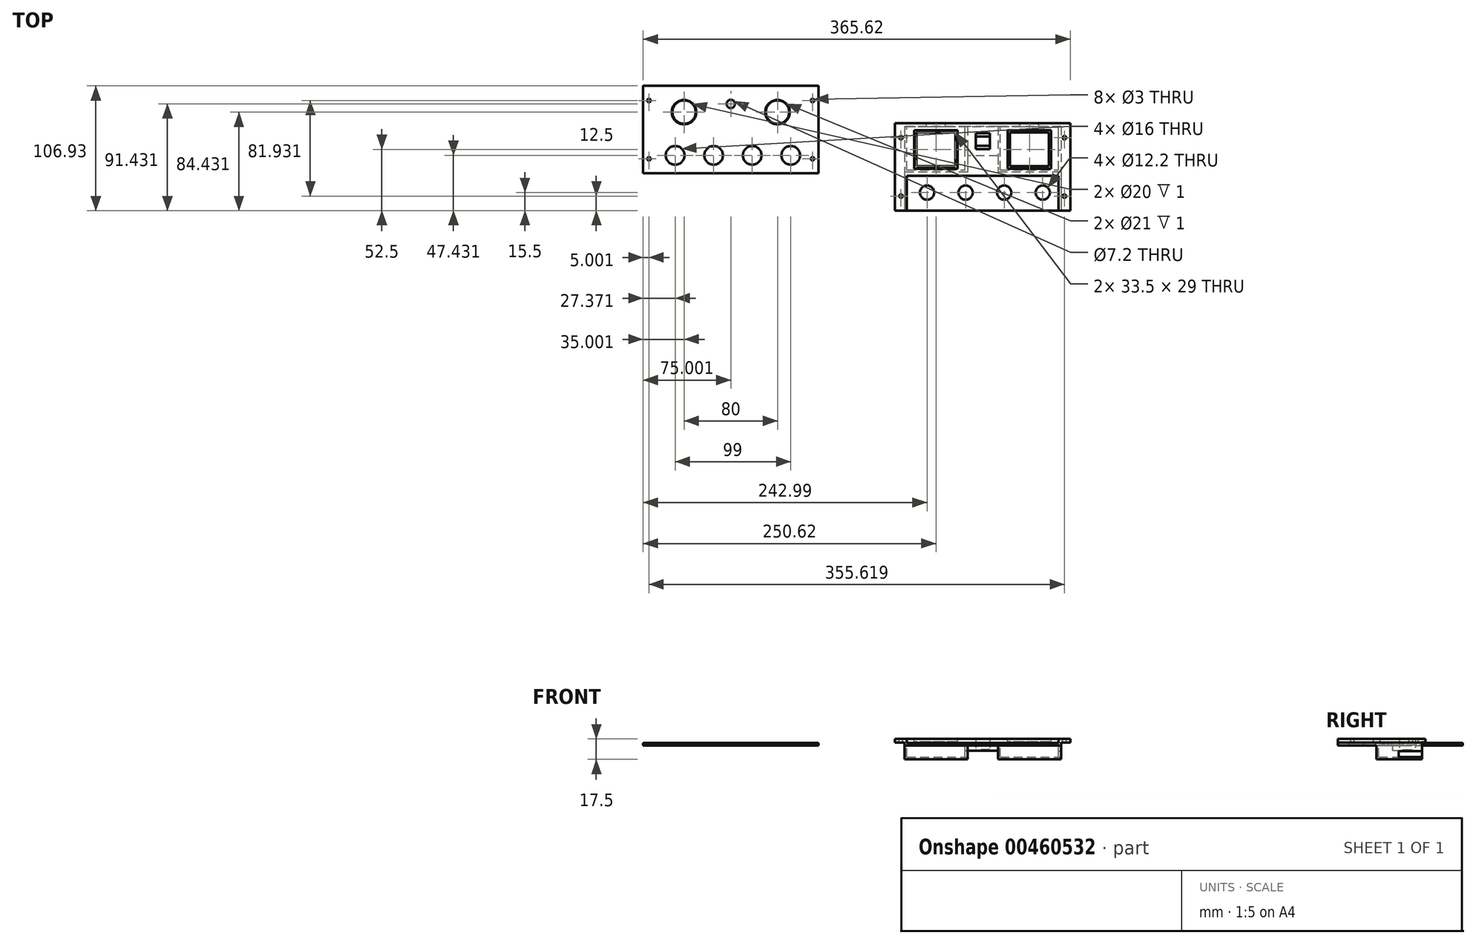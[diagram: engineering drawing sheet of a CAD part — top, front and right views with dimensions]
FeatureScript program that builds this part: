
annotation { "Feature Type Name" : "Feature", "Feature Type Description" : "" }
export const myFeature = defineFeature(function(context is Context, id is Id, definition is map)
    precondition{}
    {
        {
            var Q0;
            Q0=qCreatedBy(makeId("Top.planeOp"),FACE);
            var sketch = newSketch(context, id + "F0", { "sketchPlane" : qUnion([Q0])});
            skLineSegment(sketch, "E0.bottom", {"start": v(75, -37.5) * mm, "end": v(-75, -37.5) * mm});
            skLineSegment(sketch, "E0.top", {"start": v(75, 37.5) * mm, "end": v(-75, 37.5) * mm});
            skLineSegment(sketch, "E0.left", {"start": v(75, -37.5) * mm, "end": v(75, 37.5) * mm});
            skLineSegment(sketch, "E0.right", {"start": v(-75, -37.5) * mm, "end": v(-75, 37.5) * mm});
            skPoint(sketch, "E0.middle", {"position": v(0, 0) * mm});
            skCircle(sketch, "E1", {"center": v(0, 22) * mm, "radius": 5 * mm, "construction": true});
            skCircle(sketch, "E2", {"center": v(-47.63, -22) * mm, "radius": 6.1 * mm});
            skCircle(sketch, "E3.1.0.0", {"center": v(-14.63, -22) * mm, "radius": 6.1 * mm});
            skCircle(sketch, "E3.2.0.0", {"center": v(18.37, -22) * mm, "radius": 6.1 * mm});
            skCircle(sketch, "E3.3.0.0", {"center": v(51.37, -22) * mm, "radius": 6.1 * mm});
            skLineSegment(sketch, "E3.direction1", {"start": v(-47.63, -22) * mm, "end": v(-14.63, -22) * mm, "construction": true});
            skLineSegment(sketch, "E4.bottom", {"start": v(-75, 37.5) * mm, "end": v(-65, 37.5) * mm, "construction": true});
            skLineSegment(sketch, "E4.top", {"start": v(-75, -37.5) * mm, "end": v(-65, -37.5) * mm, "construction": true});
            skLineSegment(sketch, "E4.left", {"start": v(-75, 37.5) * mm, "end": v(-75, -37.5) * mm, "construction": true});
            skLineSegment(sketch, "E4.right", {"start": v(-65, 37.5) * mm, "end": v(-65, -37.5) * mm, "construction": true});
            skLineSegment(sketch, "E5.bottom", {"start": v(75, 37.5) * mm, "end": v(65, 37.5) * mm, "construction": true});
            skLineSegment(sketch, "E5.top", {"start": v(75, -37.5) * mm, "end": v(65, -37.5) * mm, "construction": true});
            skLineSegment(sketch, "E5.left", {"start": v(75, 37.5) * mm, "end": v(75, -37.5) * mm, "construction": true});
            skLineSegment(sketch, "E5.right", {"start": v(65, 37.5) * mm, "end": v(65, -37.5) * mm, "construction": true});
            skPoint(sketch, "E6.middle", {"position": v(-40, 15) * mm});
            skLineSegment(sketch, "E7.bottom", {"start": v(-23.25, 0.5) * mm, "end": v(-56.75, 0.5) * mm});
            skLineSegment(sketch, "E7.top", {"start": v(-23.25, 29.5) * mm, "end": v(-56.75, 29.5) * mm});
            skLineSegment(sketch, "E7.left", {"start": v(-23.25, 0.5) * mm, "end": v(-23.25, 29.5) * mm});
            skLineSegment(sketch, "E7.right", {"start": v(-56.75, 0.5) * mm, "end": v(-56.75, 29.5) * mm});
            skLineSegment(sketch, "E8.bottom", {"start": v(56.75, 0.5) * mm, "end": v(23.25, 0.5) * mm});
            skLineSegment(sketch, "E8.top", {"start": v(56.75, 29.5) * mm, "end": v(23.25, 29.5) * mm});
            skLineSegment(sketch, "E8.left", {"start": v(56.75, 0.5) * mm, "end": v(56.75, 29.5) * mm});
            skLineSegment(sketch, "E8.right", {"start": v(23.25, 0.5) * mm, "end": v(23.25, 29.5) * mm});
            skPoint(sketch, "E8.middle", {"position": v(40, 15) * mm});
            skPoint(sketch, "E9.centerSnap0", {"position": v(-70, 37.5) * mm});
            skCircle(sketch, "E10", {"center": v(-70, 25) * mm, "radius": 1.5 * mm});
            skCircle(sketch, "E11", {"center": v(-70, -25) * mm, "radius": 1.5 * mm});
            skCircle(sketch, "E12", {"center": v(70, 25) * mm, "radius": 1.5 * mm});
            skCircle(sketch, "E13", {"center": v(70, -25) * mm, "radius": 1.5 * mm});
            skLineSegment(sketch, "E14.bottom", {"start": v(6, 15.25) * mm, "end": v(-6, 15.25) * mm});
            skLineSegment(sketch, "E14.top", {"start": v(6, 28.75) * mm, "end": v(-6, 28.75) * mm});
            skLineSegment(sketch, "E14.left", {"start": v(6, 15.25) * mm, "end": v(6, 28.75) * mm});
            skLineSegment(sketch, "E14.right", {"start": v(-6, 15.25) * mm, "end": v(-6, 28.75) * mm});
            skLineSegment(sketch, "E15.bottom", {"start": v(6, 18) * mm, "end": v(-6, 18) * mm});
            skLineSegment(sketch, "E15.top", {"start": v(6, 26) * mm, "end": v(-6, 26) * mm});
            skLineSegment(sketch, "E15.left", {"start": v(6, 18) * mm, "end": v(6, 26) * mm});
            skLineSegment(sketch, "E15.right", {"start": v(-6, 18) * mm, "end": v(-6, 26) * mm});
            skSolve(sketch);
        }
        {
            var Q0;
            Q0=makeQuery(id+"F0.imprint","IMPRINT",FACE,{"disambiguationData":[TD([[makeQuery(id+"F0.imprint","IMPRINT",EDGE,{"derivedFrom":sQuery(id+"F0.wireOp",EDGE,"E0.bottom")}),-1.0]])]});
            var Q1;
            Q1=makeQuery(id+"F0.imprint","IMPRINT",FACE,{"disambiguationData":[TD([[makeQuery(id+"F0.imprint","IMPRINT",EDGE,{"derivedFrom":sQuery(id+"F0.wireOp",EDGE,"drD5jItb-HEpr-sxaA-TqkW-DfUxLCmm6Exs")}),-1.0]])]});
            var Q2;
            Q2=makeQuery(id+"F0.imprint","IMPRINT",FACE,{"disambiguationData":[TD([[makeQuery(id+"F0.imprint","IMPRINT",EDGE,{"derivedFrom":sQuery(id+"F0.wireOp",EDGE,"E15.bottom")}),-1.0]])]});
            extrude(context, id + "F1", {"entities" : qUnion([Q0, Q1, Q2]), "depth" : 2 * mm});
        }
        {
            var Q0;
            Q0=makeQuery(id+"F1.opExtrude","CAP_FACE",FACE,{"disambiguationData":[OSD([sQuery(id+"F0.wireOp",EDGE,"E0.bottom"),sQuery(id+"F0.wireOp",EDGE,"E0.top"),sQuery(id+"F0.wireOp",EDGE,"E0.left"),sQuery(id+"F0.wireOp",EDGE,"E0.right"),sQuery(id+"F0.wireOp",EDGE,"drD5jItb-HEpr-sxaA-TqkW-DfUxLCmm6Exs"),sQuery(id+"F0.wireOp",EDGE,"oSn99fef-1uPw-k3Do-L9e6-x1k65rtnndGm"),sQuery(id+"F0.wireOp",EDGE,"E1"),sQuery(id+"F0.wireOp",EDGE,"E2"),sQuery(id+"F0.wireOp",EDGE,"E3.1.0.0"),sQuery(id+"F0.wireOp",EDGE,"E3.2.0.0"),sQuery(id+"F0.wireOp",EDGE,"E3.3.0.0")])],"isStart":false});
            var sketch = newSketch(context, id + "F2", { "sketchPlane" : qUnion([Q0])});
            skLineSegment(sketch, "E16.bottom", {"start": v(-75, 37.5) * mm, "end": v(-65, 37.5) * mm});
            skLineSegment(sketch, "E16.top", {"start": v(-75, -37.5) * mm, "end": v(-65, -37.5) * mm});
            skLineSegment(sketch, "E16.left", {"start": v(-75, 37.5) * mm, "end": v(-75, -37.5) * mm});
            skLineSegment(sketch, "E16.right", {"start": v(-65, 37.5) * mm, "end": v(-65, -37.5) * mm});
            skLineSegment(sketch, "E17.bottom", {"start": v(75, -37.5) * mm, "end": v(65, -37.5) * mm});
            skLineSegment(sketch, "E17.top", {"start": v(75, 37.5) * mm, "end": v(65, 37.5) * mm});
            skLineSegment(sketch, "E17.left", {"start": v(75, -37.5) * mm, "end": v(75, 37.5) * mm});
            skLineSegment(sketch, "E17.right", {"start": v(65, -37.5) * mm, "end": v(65, 37.5) * mm});
            skSolve(sketch);
        }
        {
            var Q0;
            Q0=qSketchRegion(id+"F2",true);
            extrude(context, id + "F3", {"entities" : qUnion([Q0]), "operationType" : NewBodyOperationType.ADD, "depth" : 3.5 * mm});
        }
        {
            var Q0;
            Q0=makeQuery(id+"F3.boolean.opBoolean","MERGE",FACE,{"derivedFrom":[makeQuery(id+"F1.opExtrude","SWEPT_FACE",FACE,{"disambiguationData":[OSD([sQuery(id+"F0.wireOp",EDGE,"E0.bottom")])]}),makeQuery(id+"F3.opExtrude","SWEPT_FACE",FACE,{"disambiguationData":[OSD([sQuery(id+"F2.wireOp",EDGE,"E16.top")])]}),makeQuery(id+"F3.opExtrude","SWEPT_FACE",FACE,{"disambiguationData":[OSD([sQuery(id+"F2.wireOp",EDGE,"E17.bottom")])]})]});
            var sketch = newSketch(context, id + "F4", { "sketchPlane" : qUnion([Q0])});
            skLineSegment(sketch, "E18.bottom", {"start": v(-75, 0) * mm, "end": v(-67, 0) * mm});
            skLineSegment(sketch, "E18.top", {"start": v(-75, 2.5) * mm, "end": v(-67, 2.5) * mm});
            skLineSegment(sketch, "E18.left", {"start": v(-75, 0) * mm, "end": v(-75, 2.5) * mm});
            skLineSegment(sketch, "E18.right", {"start": v(-67, 0) * mm, "end": v(-67, 2.5) * mm});
            skLineSegment(sketch, "E19.bottom", {"start": v(75, 0) * mm, "end": v(67, 0) * mm});
            skLineSegment(sketch, "E19.top", {"start": v(75, 2.5) * mm, "end": v(67, 2.5) * mm});
            skLineSegment(sketch, "E19.left", {"start": v(75, 0) * mm, "end": v(75, 2.5) * mm});
            skLineSegment(sketch, "E19.right", {"start": v(67, 0) * mm, "end": v(67, 2.5) * mm});
            skSolve(sketch);
        }
        {
            var Q0;
            Q0=qSketchRegion(id+"F4",true);
            extrude(context, id + "F5", {"entities" : qUnion([Q0]), "operationType" : NewBodyOperationType.REMOVE, "oppositeDirection" : true, "depth" : 80 * mm});
        }
        {
            var Q0;
            Q0=makeQuery(id+"F1.opExtrude","CAP_FACE",FACE,{"disambiguationData":[OSD([sQuery(id+"F0.wireOp",EDGE,"E0.bottom"),sQuery(id+"F0.wireOp",EDGE,"E0.top"),sQuery(id+"F0.wireOp",EDGE,"E0.left"),sQuery(id+"F0.wireOp",EDGE,"E0.right"),sQuery(id+"F0.wireOp",EDGE,"drD5jItb-HEpr-sxaA-TqkW-DfUxLCmm6Exs"),sQuery(id+"F0.wireOp",EDGE,"oSn99fef-1uPw-k3Do-L9e6-x1k65rtnndGm"),sQuery(id+"F0.wireOp",EDGE,"E1"),sQuery(id+"F0.wireOp",EDGE,"E2"),sQuery(id+"F0.wireOp",EDGE,"E3.1.0.0"),sQuery(id+"F0.wireOp",EDGE,"E3.2.0.0"),sQuery(id+"F0.wireOp",EDGE,"E3.3.0.0")])],"isStart":false});
            var sketch = newSketch(context, id + "F6", { "sketchPlane" : qUnion([Q0])});
            skLineSegment(sketch, "E20.bottom", {"start": v(-65, 37.5) * mm, "end": v(65, 37.5) * mm});
            skLineSegment(sketch, "E20.top", {"start": v(-65, -7.5) * mm, "end": v(65, -7.5) * mm});
            skLineSegment(sketch, "E20.left", {"start": v(-65, 37.5) * mm, "end": v(-65, -7.5) * mm});
            skLineSegment(sketch, "E20.right", {"start": v(65, 37.5) * mm, "end": v(65, -7.5) * mm});
            skCircle(sketch, "E21", {"center": v(0, 22) * mm, "radius": 5 * mm, "construction": true});
            skLineSegment(sketch, "E22.bottom", {"start": v(-23.25, 0.5) * mm, "end": v(-56.75, 0.5) * mm});
            skLineSegment(sketch, "E22.top", {"start": v(-23.25, 29.5) * mm, "end": v(-56.75, 29.5) * mm});
            skLineSegment(sketch, "E22.left", {"start": v(-23.25, 0.5) * mm, "end": v(-23.25, 29.5) * mm});
            skLineSegment(sketch, "E22.right", {"start": v(-56.75, 0.5) * mm, "end": v(-56.75, 29.5) * mm});
            skPoint(sketch, "E22.middle", {"position": v(-40, 15) * mm});
            skLineSegment(sketch, "E23.bottom", {"start": v(56.75, 0.5) * mm, "end": v(23.25, 0.5) * mm});
            skLineSegment(sketch, "E23.top", {"start": v(56.75, 29.5) * mm, "end": v(23.25, 29.5) * mm});
            skLineSegment(sketch, "E23.left", {"start": v(56.75, 0.5) * mm, "end": v(56.75, 29.5) * mm});
            skLineSegment(sketch, "E23.right", {"start": v(23.25, 0.5) * mm, "end": v(23.25, 29.5) * mm});
            skPoint(sketch, "E23.middle", {"position": v(40, 15) * mm});
            skLineSegment(sketch, "E24.bottom", {"start": v(6, 15.25) * mm, "end": v(-6, 15.25) * mm});
            skLineSegment(sketch, "E24.top", {"start": v(6, 28.75) * mm, "end": v(-6, 28.75) * mm});
            skLineSegment(sketch, "E24.left", {"start": v(6, 15.25) * mm, "end": v(6, 28.75) * mm});
            skLineSegment(sketch, "E24.right", {"start": v(-6, 15.25) * mm, "end": v(-6, 28.75) * mm});
            skSolve(sketch);
        }
        {
            var Q0;
            Q0=qSketchRegion(id+"F6",true);
            extrude(context, id + "F7", {"entities" : qUnion([Q0]), "operationType" : NewBodyOperationType.ADD, "depth" : 3.5 * mm});
        }
        {
            var Q0;
            Q0=makeQuery(id+"F7.boolean.opBoolean","MERGE",FACE,{"derivedFrom":[makeQuery(id+"F3.opExtrude","CAP_FACE",FACE,{"disambiguationData":[OSD([sQuery(id+"F2.wireOp",EDGE,"E16.bottom"),sQuery(id+"F2.wireOp",EDGE,"E16.top"),sQuery(id+"F2.wireOp",EDGE,"E16.left"),sQuery(id+"F2.wireOp",EDGE,"E16.right")])],"isStart":false}),makeQuery(id+"F3.opExtrude","CAP_FACE",FACE,{"disambiguationData":[OSD([sQuery(id+"F2.wireOp",EDGE,"E17.bottom"),sQuery(id+"F2.wireOp",EDGE,"E17.top"),sQuery(id+"F2.wireOp",EDGE,"E17.left"),sQuery(id+"F2.wireOp",EDGE,"E17.right")])],"isStart":false}),makeQuery(id+"F7.opExtrude","CAP_FACE",FACE,{"disambiguationData":[OSD([sQuery(id+"F6.wireOp",EDGE,"E20.bottom"),sQuery(id+"F6.wireOp",EDGE,"E20.top"),sQuery(id+"F6.wireOp",EDGE,"E20.left"),sQuery(id+"F6.wireOp",EDGE,"E20.right"),sQuery(id+"F6.wireOp",EDGE,"H2Zb9yD0-p2Z7-Kh5e-a6hj-aLUdcpXocAIw"),sQuery(id+"F6.wireOp",EDGE,"7ZJ2aJG6-LJXW-fwXF-v4kC-qdLRGwjfnqPK"),sQuery(id+"F6.wireOp",EDGE,"E21")])],"isStart":false})]});
            var sketch = newSketch(context, id + "F8", { "sketchPlane" : qUnion([Q0])});
            skLineSegment(sketch, "E25.bottom", {"start": v(-21.4, -1.5) * mm, "end": v(-58.6, -1.5) * mm});
            skLineSegment(sketch, "E25.top", {"start": v(-21.4, 31.5) * mm, "end": v(-58.6, 31.5) * mm});
            skLineSegment(sketch, "E25.left", {"start": v(-21.4, -1.5) * mm, "end": v(-21.4, 31.5) * mm});
            skLineSegment(sketch, "E25.right", {"start": v(-58.6, -1.5) * mm, "end": v(-58.6, 31.5) * mm});
            skPoint(sketch, "E25.middle", {"position": v(-40, 15) * mm});
            skLineSegment(sketch, "E26.bottom", {"start": v(58.6, -1.5) * mm, "end": v(21.4, -1.5) * mm});
            skLineSegment(sketch, "E26.top", {"start": v(58.6, 31.5) * mm, "end": v(21.4, 31.5) * mm});
            skLineSegment(sketch, "E26.left", {"start": v(58.6, -1.5) * mm, "end": v(58.6, 31.5) * mm});
            skLineSegment(sketch, "E26.right", {"start": v(21.4, -1.5) * mm, "end": v(21.4, 31.5) * mm});
            skPoint(sketch, "E26.middle", {"position": v(40, 15) * mm});
            skLineSegment(sketch, "E27.bottom", {"start": v(-32, 31.5) * mm, "end": v(-48, 31.5) * mm});
            skLineSegment(sketch, "E27.top", {"start": v(-32, 46.5) * mm, "end": v(-48, 46.5) * mm});
            skLineSegment(sketch, "E27.left", {"start": v(-32, 31.5) * mm, "end": v(-32, 46.5) * mm});
            skLineSegment(sketch, "E27.right", {"start": v(-48, 31.5) * mm, "end": v(-48, 46.5) * mm});
            skPoint(sketch, "E27.middle", {"position": v(-40, 39) * mm});
            skPoint(sketch, "E27.middle.positionSnap0", {"position": v(-40, 31.5) * mm});
            skPoint(sketch, "E27.centerSnap0", {"position": v(-40, 31.5) * mm});
            skLineSegment(sketch, "E28.bottom", {"start": v(48, 31.5) * mm, "end": v(32, 31.5) * mm});
            skLineSegment(sketch, "E28.top", {"start": v(48, 46.5) * mm, "end": v(32, 46.5) * mm});
            skLineSegment(sketch, "E28.left", {"start": v(48, 31.5) * mm, "end": v(48, 46.5) * mm});
            skLineSegment(sketch, "E28.right", {"start": v(32, 31.5) * mm, "end": v(32, 46.5) * mm});
            skPoint(sketch, "E28.middle", {"position": v(40, 39) * mm});
            skPoint(sketch, "E28.middle.positionSnap0", {"position": v(40, 31.5) * mm});
            skPoint(sketch, "E28.centerSnap0", {"position": v(40, 31.5) * mm});
            skSolve(sketch);
        }
        {
            var Q0;
            Q0=makeQuery(id+"F8.imprint","IMPRINT",FACE,{"disambiguationData":[TD([[makeQuery(id+"F8.imprint","IMPRINT",EDGE,{"derivedFrom":sQuery(id+"F8.wireOp",EDGE,"E25.bottom")}),-1.0]])]});
            var Q1;
            Q1=makeQuery(id+"F8.imprint","IMPRINT",FACE,{"disambiguationData":[TD([[makeQuery(id+"F8.imprint","IMPRINT",EDGE,{"derivedFrom":sQuery(id+"F8.wireOp",EDGE,"E26.bottom")}),-1.0]])]});
            var Q2;
            {var subQ0=sQuery(id+"F8.wireOp",EDGE,"E27.top");Q2=makeQuery(id+"F8.imprint","IMPRINT",FACE,{"disambiguationData":[TD([[makeQuery(id+"F8.imprint","IMPRINT",EDGE,{"derivedFrom":subQ0}),1.0]])]});}
            var Q3;
            {var subQ0=sQuery(id+"F8.wireOp",EDGE,"E28.top");Q3=makeQuery(id+"F8.imprint","IMPRINT",FACE,{"disambiguationData":[TD([[makeQuery(id+"F8.imprint","IMPRINT",EDGE,{"derivedFrom":subQ0}),1.0]])]});}
            var Q4;
            {var subQ0=sQuery(id+"F8.wireOp",EDGE,"E27.bottom");Q4=makeQuery(id+"F8.imprint","IMPRINT",FACE,{"disambiguationData":[TD([[makeQuery(id+"F8.imprint","IMPRINT",EDGE,{"derivedFrom":subQ0}),-1.0]])]});}
            var Q5;
            {var subQ0=sQuery(id+"F8.wireOp",EDGE,"E28.bottom");Q5=makeQuery(id+"F8.imprint","IMPRINT",FACE,{"disambiguationData":[TD([[makeQuery(id+"F8.imprint","IMPRINT",EDGE,{"derivedFrom":subQ0}),-1.0]])]});}
            extrude(context, id + "F9", {"entities" : qUnion([Q0, Q1, Q2, Q3, Q4, Q5]), "operationType" : NewBodyOperationType.REMOVE, "oppositeDirection" : true, "depth" : 2.5 * mm});
        }
        {
            var Q0;
            Q0=qCreatedBy(makeId("Top.planeOp"),FACE);
            var sketch = newSketch(context, id + "F10", { "sketchPlane" : qUnion([Q0])});
            skLineSegment(sketch, "E29.bottom", {"start": v(-140.62, -5.57) * mm, "end": v(-290.62, -5.57) * mm});
            skLineSegment(sketch, "E29.top", {"start": v(-140.62, 69.43) * mm, "end": v(-290.62, 69.43) * mm});
            skLineSegment(sketch, "E29.left", {"start": v(-140.62, -5.57) * mm, "end": v(-140.62, 69.43) * mm});
            skLineSegment(sketch, "E29.right", {"start": v(-290.62, -5.57) * mm, "end": v(-290.62, 69.43) * mm});
            skPoint(sketch, "E29.middle", {"position": v(-215.62, 31.93) * mm});
            skCircle(sketch, "E30", {"center": v(-215.62, 53.93) * mm, "radius": 3.6 * mm});
            skCircle(sketch, "E31", {"center": v(-263.25, 9.93) * mm, "radius": 8 * mm});
            skCircle(sketch, "E32.1.0.0", {"center": v(-230.25, 9.93) * mm, "radius": 8 * mm});
            skCircle(sketch, "E32.2.0.0", {"center": v(-197.25, 9.93) * mm, "radius": 8 * mm});
            skCircle(sketch, "E32.3.0.0", {"center": v(-164.25, 9.93) * mm, "radius": 8 * mm});
            skLineSegment(sketch, "E32.direction1", {"start": v(-263.25, 9.93) * mm, "end": v(-230.25, 9.93) * mm, "construction": true});
            skLineSegment(sketch, "E33.bottom", {"start": v(-290.62, 69.43) * mm, "end": v(-280.62, 69.43) * mm, "construction": true});
            skLineSegment(sketch, "E33.top", {"start": v(-290.62, -5.57) * mm, "end": v(-280.62, -5.57) * mm, "construction": true});
            skLineSegment(sketch, "E33.left", {"start": v(-290.62, 69.43) * mm, "end": v(-290.62, -5.57) * mm, "construction": true});
            skLineSegment(sketch, "E33.right", {"start": v(-280.62, 69.43) * mm, "end": v(-280.62, -5.57) * mm, "construction": true});
            skLineSegment(sketch, "E34.bottom", {"start": v(-140.62, 69.43) * mm, "end": v(-150.62, 69.43) * mm, "construction": true});
            skLineSegment(sketch, "E34.top", {"start": v(-140.62, -5.57) * mm, "end": v(-150.62, -5.57) * mm, "construction": true});
            skLineSegment(sketch, "E34.left", {"start": v(-140.62, 69.43) * mm, "end": v(-140.62, -5.57) * mm, "construction": true});
            skLineSegment(sketch, "E34.right", {"start": v(-150.62, 69.43) * mm, "end": v(-150.62, -5.57) * mm, "construction": true});
            skPoint(sketch, "E35.middle", {"position": v(-255.62, 46.93) * mm});
            skPoint(sketch, "E36.middle", {"position": v(-175.62, 46.93) * mm});
            skCircle(sketch, "E37", {"center": v(-255.62, 46.93) * mm, "radius": 10 * mm});
            skCircle(sketch, "E38", {"center": v(-175.62, 46.93) * mm, "radius": 10 * mm});
            skLineSegment(sketch, "E39.bottom", {"start": v(-236.87, 30.43) * mm, "end": v(-274.37, 30.43) * mm, "construction": true});
            skLineSegment(sketch, "E39.top", {"start": v(-236.87, 63.43) * mm, "end": v(-274.37, 63.43) * mm, "construction": true});
            skLineSegment(sketch, "E39.left", {"start": v(-236.87, 30.43) * mm, "end": v(-236.87, 63.43) * mm, "construction": true});
            skLineSegment(sketch, "E39.right", {"start": v(-274.37, 30.43) * mm, "end": v(-274.37, 63.43) * mm, "construction": true});
            skLineSegment(sketch, "E40.bottom", {"start": v(-156.87, 30.43) * mm, "end": v(-194.37, 30.43) * mm, "construction": true});
            skLineSegment(sketch, "E40.top", {"start": v(-156.87, 63.43) * mm, "end": v(-194.37, 63.43) * mm, "construction": true});
            skLineSegment(sketch, "E40.left", {"start": v(-156.87, 30.43) * mm, "end": v(-156.87, 63.43) * mm, "construction": true});
            skLineSegment(sketch, "E40.right", {"start": v(-194.37, 30.43) * mm, "end": v(-194.37, 63.43) * mm, "construction": true});
            skCircle(sketch, "E41", {"center": v(-285.62, 56.93) * mm, "radius": 1.5 * mm});
            skCircle(sketch, "E42", {"center": v(-285.62, 6.93) * mm, "radius": 1.5 * mm});
            skCircle(sketch, "E43", {"center": v(-145.62, 56.93) * mm, "radius": 1.5 * mm});
            skCircle(sketch, "E44", {"center": v(-145.62, 6.93) * mm, "radius": 1.5 * mm});
            skSolve(sketch);
        }
        {
            var Q0;
            Q0=makeQuery(id+"F10.imprint","IMPRINT",FACE,{"disambiguationData":[TD([[makeQuery(id+"F10.imprint","IMPRINT",EDGE,{"derivedFrom":sQuery(id+"F10.wireOp",EDGE,"E29.bottom")}),-1.0]])]});
            extrude(context, id + "F11", {"entities" : qUnion([Q0]), "depth" : 2 * mm});
        }
        {
            var Q0;
            Q0=makeQuery(id+"F11.opExtrude","CAP_FACE",FACE,{"disambiguationData":[OSD([sQuery(id+"F10.wireOp",EDGE,"E29.bottom"),sQuery(id+"F10.wireOp",EDGE,"E29.top"),sQuery(id+"F10.wireOp",EDGE,"E29.left"),sQuery(id+"F10.wireOp",EDGE,"E29.right"),sQuery(id+"F10.wireOp",EDGE,"E30"),sQuery(id+"F10.wireOp",EDGE,"E31"),sQuery(id+"F10.wireOp",EDGE,"E32.1.0.0"),sQuery(id+"F10.wireOp",EDGE,"E32.2.0.0"),sQuery(id+"F10.wireOp",EDGE,"E32.3.0.0"),sQuery(id+"F10.wireOp",EDGE,"E37"),sQuery(id+"F10.wireOp",EDGE,"E38")])],"isStart":false});
            var sketch = newSketch(context, id + "F12", { "sketchPlane" : qUnion([Q0])});
            skLineSegment(sketch, "E45.bottom", {"start": v(-239.12, 65.68) * mm, "end": v(-272.12, 65.68) * mm, "construction": true});
            skLineSegment(sketch, "E45.top", {"start": v(-239.12, 28.18) * mm, "end": v(-272.12, 28.18) * mm, "construction": true});
            skLineSegment(sketch, "E45.left", {"start": v(-239.12, 65.68) * mm, "end": v(-239.12, 28.18) * mm, "construction": true});
            skLineSegment(sketch, "E45.right", {"start": v(-272.12, 65.68) * mm, "end": v(-272.12, 28.18) * mm, "construction": true});
            skPoint(sketch, "E45.middle", {"position": v(-255.62, 46.93) * mm});
            skLineSegment(sketch, "E46.bottom", {"start": v(-159.12, 65.68) * mm, "end": v(-192.12, 65.68) * mm, "construction": true});
            skLineSegment(sketch, "E46.top", {"start": v(-159.12, 28.18) * mm, "end": v(-192.12, 28.18) * mm, "construction": true});
            skLineSegment(sketch, "E46.left", {"start": v(-159.12, 65.68) * mm, "end": v(-159.12, 28.18) * mm, "construction": true});
            skLineSegment(sketch, "E46.right", {"start": v(-192.12, 65.68) * mm, "end": v(-192.12, 28.18) * mm, "construction": true});
            skPoint(sketch, "E46.middle", {"position": v(-175.62, 46.93) * mm});
            skCircle(sketch, "E47", {"center": v(-255.62, 46.93) * mm, "radius": 10.5 * mm});
            skCircle(sketch, "E48", {"center": v(-175.62, 46.93) * mm, "radius": 10.5 * mm});
            skSolve(sketch);
        }
        {
            var Q0;
            Q0 = qSketchRegion(id + "F12", true);
            extrude(context, id + "F13", {"entities" : qUnion([Q0]), "operationType" : NewBodyOperationType.REMOVE, "oppositeDirection" : true, "depth" : 1 * mm});
        }
        {
            var Q0;
            Q0=makeQuery(id+"F0.imprint","IMPRINT",FACE,{"disambiguationData":[TD([[makeQuery(id+"F0.imprint","IMPRINT",EDGE,{"derivedFrom":sQuery(id+"F0.wireOp",EDGE,"E0.bottom")}),-1.0]])]});
            var sketch = newSketch(context, id + "F14", { "sketchPlane" : qUnion([Q0])});
            skPoint(sketch, "E49.0", {"position": v(0, 22) * mm});
            skLineSegment(sketch, "E50.bottom", {"start": v(13, 34.5) * mm, "end": v(-13, 34.5) * mm});
            skLineSegment(sketch, "E50.top", {"start": v(13, 9.5) * mm, "end": v(-13, 9.5) * mm});
            skLineSegment(sketch, "E50.left", {"start": v(13, 34.5) * mm, "end": v(13, 9.5) * mm});
            skLineSegment(sketch, "E50.right", {"start": v(-13, 34.5) * mm, "end": v(-13, 9.5) * mm});
            skPoint(sketch, "E51.0", {"position": v(6, 26) * mm});
            skLineSegment(sketch, "E52.bottom", {"start": v(6, 26) * mm, "end": v(-6, 26) * mm});
            skLineSegment(sketch, "E52.top", {"start": v(6, 18) * mm, "end": v(-6, 18) * mm});
            skLineSegment(sketch, "E52.left", {"start": v(6, 26) * mm, "end": v(6, 18) * mm});
            skLineSegment(sketch, "E52.right", {"start": v(-6, 26) * mm, "end": v(-6, 18) * mm});
            skSolve(sketch);
        }
        {
            var Q0;
            Q0=makeQuery(id+"F14.imprint","IMPRINT",FACE,{"disambiguationData":[TD([[makeQuery(id+"F14.imprint","IMPRINT",EDGE,{"derivedFrom":sQuery(id+"F14.wireOp",EDGE,"E50.bottom")}),1.0]])]});
            var Q1;
            Q1=makeQuery(id+"F0.imprint","IMPRINT",FACE,{"disambiguationData":[TD([[makeQuery(id+"F0.imprint","IMPRINT",EDGE,{"derivedFrom":sQuery(id+"F0.wireOp",EDGE,"E15.bottom")}),-1.0]])]});
            extrude(context, id + "F15", {"entities" : qUnion([Q0, Q1]), "operationType" : NewBodyOperationType.ADD, "oppositeDirection" : true, "depth" : 4.5 * mm});
        }
        {
            var Q0;
            Q0=makeQuery(id+"F7.boolean.opBoolean","MERGE",FACE,{"derivedFrom":[makeQuery(id+"F3.opExtrude","CAP_FACE",FACE,{"disambiguationData":[OSD([sQuery(id+"F2.wireOp",EDGE,"E16.bottom"),sQuery(id+"F2.wireOp",EDGE,"E16.top"),sQuery(id+"F2.wireOp",EDGE,"E16.left"),sQuery(id+"F2.wireOp",EDGE,"E16.right")])],"isStart":false}),makeQuery(id+"F3.opExtrude","CAP_FACE",FACE,{"disambiguationData":[OSD([sQuery(id+"F2.wireOp",EDGE,"E17.bottom"),sQuery(id+"F2.wireOp",EDGE,"E17.top"),sQuery(id+"F2.wireOp",EDGE,"E17.left"),sQuery(id+"F2.wireOp",EDGE,"E17.right")])],"isStart":false}),makeQuery(id+"F7.opExtrude","CAP_FACE",FACE,{"disambiguationData":[OSD([sQuery(id+"F6.wireOp",EDGE,"E20.bottom"),sQuery(id+"F6.wireOp",EDGE,"E20.top"),sQuery(id+"F6.wireOp",EDGE,"E20.left"),sQuery(id+"F6.wireOp",EDGE,"E20.right"),sQuery(id+"F6.wireOp",EDGE,"E22.bottom"),sQuery(id+"F6.wireOp",EDGE,"E22.top"),sQuery(id+"F6.wireOp",EDGE,"E22.left"),sQuery(id+"F6.wireOp",EDGE,"E22.right"),sQuery(id+"F6.wireOp",EDGE,"E23.bottom"),sQuery(id+"F6.wireOp",EDGE,"E23.top"),sQuery(id+"F6.wireOp",EDGE,"E23.left"),sQuery(id+"F6.wireOp",EDGE,"E23.right"),sQuery(id+"F6.wireOp",EDGE,"E24.bottom"),sQuery(id+"F6.wireOp",EDGE,"E24.top"),sQuery(id+"F6.wireOp",EDGE,"E24.left"),sQuery(id+"F6.wireOp",EDGE,"E24.right")])],"isStart":false})]});
            var sketch = newSketch(context, id + "F16", { "sketchPlane" : qUnion([Q0])});
            skPoint(sketch, "E53.0", {"position": v(0, 22) * mm});
            skLineSegment(sketch, "E54.bottom", {"start": v(6, 15.25) * mm, "end": v(-6, 15.25) * mm});
            skLineSegment(sketch, "E54.top", {"start": v(6, 28.75) * mm, "end": v(-6, 28.75) * mm});
            skLineSegment(sketch, "E54.left", {"start": v(6, 15.25) * mm, "end": v(6, 28.75) * mm});
            skLineSegment(sketch, "E54.right", {"start": v(-6, 15.25) * mm, "end": v(-6, 28.75) * mm});
            skSolve(sketch);
        }
        {
            var Q0;
            Q0 = qSketchRegion(id + "F16", true);
            extrude(context, id + "F17", {"entities" : qUnion([Q0]), "operationType" : NewBodyOperationType.REMOVE, "oppositeDirection" : true, "depth" : 9 * mm});
        }
        {
            var Q0;
            Q0=makeQuery(id+"F0.imprint","IMPRINT",FACE,{"disambiguationData":[TD([[makeQuery(id+"F0.imprint","IMPRINT",EDGE,{"derivedFrom":sQuery(id+"F0.wireOp",EDGE,"E0.bottom")}),-1.0]])]});
            var sketch = newSketch(context, id + "F18", { "sketchPlane" : qUnion([Q0])});
            skPoint(sketch, "E55.0", {"position": v(-67, 37.5) * mm});
            skPoint(sketch, "E55.1", {"position": v(67, 37.5) * mm});
            skLineSegment(sketch, "E56.bottom", {"start": v(-67, 37.5) * mm, "end": v(67, 37.5) * mm});
            skLineSegment(sketch, "E56.top", {"start": v(-67, 34.5) * mm, "end": v(67, 34.5) * mm});
            skLineSegment(sketch, "E56.left", {"start": v(-67, 37.5) * mm, "end": v(-67, 34.5) * mm});
            skLineSegment(sketch, "E56.right", {"start": v(67, 37.5) * mm, "end": v(67, 34.5) * mm});
            skSolve(sketch);
        }
        {
            var Q0;
            Q0=makeQuery(id+"F18.imprint","IMPRINT",FACE,{"disambiguationData":[TD([[makeQuery(id+"F18.imprint","IMPRINT",EDGE,{"derivedFrom":sQuery(id+"F18.wireOp",EDGE,"E56.bottom")}),1.0]])]});
            extrude(context, id + "F19", {"entities" : qUnion([Q0]), "operationType" : NewBodyOperationType.REMOVE, "depth" : 2.5 * mm});
        }
        {
            var Q0;
            Q0=makeQuery(id+"F0.imprint","IMPRINT",FACE,{"disambiguationData":[TD([[makeQuery(id+"F0.imprint","IMPRINT",EDGE,{"derivedFrom":sQuery(id+"F0.wireOp",EDGE,"E0.bottom")}),-1.0]])]});
            var sketch = newSketch(context, id + "F20", { "sketchPlane" : qUnion([Q0])});
            skPoint(sketch, "E57.0", {"position": v(-40, 15) * mm});
            skPoint(sketch, "E57.1", {"position": v(40, 15) * mm});
            skLineSegment(sketch, "E58.bottom", {"start": v(-13, 34.5) * mm, "end": v(-67, 34.5) * mm});
            skLineSegment(sketch, "E58.top", {"start": v(-13, -4.5) * mm, "end": v(-67, -4.5) * mm});
            skLineSegment(sketch, "E58.left", {"start": v(-13, 34.5) * mm, "end": v(-13, -4.5) * mm});
            skLineSegment(sketch, "E58.right", {"start": v(-67, 34.5) * mm, "end": v(-67, -4.5) * mm});
            skLineSegment(sketch, "E59.bottom", {"start": v(67, 34.5) * mm, "end": v(13, 34.5) * mm});
            skLineSegment(sketch, "E59.top", {"start": v(67, -4.5) * mm, "end": v(13, -4.5) * mm});
            skLineSegment(sketch, "E59.left", {"start": v(67, 34.5) * mm, "end": v(67, -4.5) * mm});
            skLineSegment(sketch, "E59.right", {"start": v(13, 34.5) * mm, "end": v(13, -4.5) * mm});
            skSolve(sketch);
        }
        {
            var Q0;
            Q0=makeQuery(id+"F20.imprint","IMPRINT",FACE,{"disambiguationData":[TD([[makeQuery(id+"F20.imprint","IMPRINT",EDGE,{"derivedFrom":sQuery(id+"F20.wireOp",EDGE,"E59.bottom")}),1.0]])]});
            var Q1;
            Q1=makeQuery(id+"F20.imprint","IMPRINT",FACE,{"disambiguationData":[TD([[makeQuery(id+"F20.imprint","IMPRINT",EDGE,{"derivedFrom":sQuery(id+"F20.wireOp",EDGE,"E58.bottom")}),1.0]])]});
            var Q2;
            Q2=makeQuery(id+"F20.imprint","IMPRINT",FACE,{"disambiguationData":[TD([[makeQuery(id+"F20.imprint","IMPRINT",EDGE,{"derivedFrom":makeQuery(id+"F0.imprint","IMPRINT",EDGE,{"derivedFrom":sQuery(id+"F0.wireOp",EDGE,"E8.bottom")})}),-1.0]])]});
            var Q3;
            Q3=makeQuery(id+"F20.imprint","IMPRINT",FACE,{"disambiguationData":[TD([[makeQuery(id+"F20.imprint","IMPRINT",EDGE,{"derivedFrom":makeQuery(id+"F0.imprint","IMPRINT",EDGE,{"derivedFrom":sQuery(id+"F0.wireOp",EDGE,"E7.bottom")})}),-1.0]])]});
            extrude(context, id + "F21", {"entities" : qUnion([Q0, Q1, Q2, Q3]), "operationType" : NewBodyOperationType.ADD, "oppositeDirection" : true, "depth" : 12 * mm});
        }
        {
            var Q0;
            Q0=makeQuery(id+"F21.boolean.opBoolean","MERGE",FACE,{"derivedFrom":[makeQuery(id+"F19.boolean.opBoolean","MERGE",FACE,{"derivedFrom":[makeQuery(id+"F15.opExtrude","SWEPT_FACE",FACE,{"disambiguationData":[OSD([sQuery(id+"F14.wireOp",EDGE,"E50.bottom")])]}),makeQuery(id+"F19.opExtrude","SWEPT_FACE",FACE,{"disambiguationData":[OSD([sQuery(id+"F18.wireOp",EDGE,"E56.top")])]})]}),makeQuery(id+"F21.opExtrude","SWEPT_FACE",FACE,{"disambiguationData":[OSD([sQuery(id+"F20.wireOp",EDGE,"E58.bottom")])]}),makeQuery(id+"F21.opExtrude","SWEPT_FACE",FACE,{"disambiguationData":[OSD([sQuery(id+"F20.wireOp",EDGE,"E59.bottom")])]})]});
            var sketch = newSketch(context, id + "F22", { "sketchPlane" : qUnion([Q0])});
            skLineSegment(sketch, "E60.bottom", {"start": v(-15, -10) * mm, "end": v(-65, -10) * mm});
            skLineSegment(sketch, "E60.top", {"start": v(-15, 0.5) * mm, "end": v(-65, 0.5) * mm});
            skLineSegment(sketch, "E60.left", {"start": v(-15, -10) * mm, "end": v(-15, 0.5) * mm});
            skLineSegment(sketch, "E60.right", {"start": v(-65, -10) * mm, "end": v(-65, 0.5) * mm});
            skPoint(sketch, "E60.middle", {"position": v(-40, -4.75) * mm});
            skPoint(sketch, "E60.middle.positionSnap0", {"position": v(-40, -12) * mm});
            skPoint(sketch, "E60.middle.positionSnap1", {"position": v(-67, -4.75) * mm});
            skPoint(sketch, "E60.centerSnap0", {"position": v(-40, -12) * mm});
            skPoint(sketch, "E60.centerSnap1", {"position": v(-67, -4.75) * mm});
            skLineSegment(sketch, "E61.bottom", {"start": v(65, -10) * mm, "end": v(15, -10) * mm});
            skLineSegment(sketch, "E61.top", {"start": v(65, 0.5) * mm, "end": v(15, 0.5) * mm});
            skLineSegment(sketch, "E61.left", {"start": v(65, -10) * mm, "end": v(65, 0.5) * mm});
            skLineSegment(sketch, "E61.right", {"start": v(15, -10) * mm, "end": v(15, 0.5) * mm});
            skPoint(sketch, "E61.middle", {"position": v(40, -4.75) * mm});
            skPoint(sketch, "E61.middle.positionSnap0", {"position": v(40, -12) * mm});
            skPoint(sketch, "E61.middle.positionSnap1", {"position": v(67, -4.75) * mm});
            skPoint(sketch, "E61.centerSnap0", {"position": v(40, -12) * mm});
            skPoint(sketch, "E61.centerSnap1", {"position": v(67, -4.75) * mm});
            skSolve(sketch);
        }
        {
            var Q0;
            Q0 = qSketchRegion(id + "F22", true);
            extrude(context, id + "F23", {"entities" : qUnion([Q0]), "operationType" : NewBodyOperationType.REMOVE, "oppositeDirection" : true, "depth" : 37 * mm});
        }
        {
            var Q0;
            Q0=makeQuery(id+"F16.imprint","IMPRINT",FACE,{"disambiguationData":[TD([[makeQuery(id+"F16.imprint","IMPRINT",EDGE,{"derivedFrom":sQuery(id+"F16.wireOp",EDGE,"E54.bottom")}),1.0]])]});
            var sketch = newSketch(context, id + "F24", { "sketchPlane" : qUnion([Q0])});
            skPoint(sketch, "E62.0", {"position": v(-70, 25) * mm});
            skPoint(sketch, "E62.1", {"position": v(-70, -25) * mm});
            skPoint(sketch, "E62.2", {"position": v(70, -25) * mm});
            skPoint(sketch, "E62.3", {"position": v(70, 25) * mm});
            skCircle(sketch, "E63", {"center": v(-70, 25) * mm, "radius": 1.5 * mm});
            skCircle(sketch, "E64", {"center": v(-70, -25) * mm, "radius": 1.5 * mm});
            skCircle(sketch, "E65", {"center": v(70, 25) * mm, "radius": 1.5 * mm});
            skCircle(sketch, "E66", {"center": v(70, -25) * mm, "radius": 1.5 * mm});
            skSolve(sketch);
        }
        {
            var Q0;
            Q0 = qSketchRegion(id + "F24", true);
            extrude(context, id + "F25", {"entities" : qUnion([Q0]), "operationType" : NewBodyOperationType.REMOVE, "oppositeDirection" : true, "depth" : 25 * mm});
        }
        {
            var Q0;
            Q0=makeQuery(id+"F9.boolean.opBoolean","COPY",FACE,{"derivedFrom":makeQuery(id+"F9.opExtrude","CAP_FACE",FACE,{"disambiguationData":[OSD([sQuery(id+"F6.wireOp",EDGE,"E22.bottom"),sQuery(id+"F6.wireOp",EDGE,"E22.top"),sQuery(id+"F6.wireOp",EDGE,"E22.left"),sQuery(id+"F6.wireOp",EDGE,"E22.right"),sQuery(id+"F8.wireOp",EDGE,"E25.bottom"),sQuery(id+"F8.wireOp",EDGE,"E25.top"),sQuery(id+"F8.wireOp",EDGE,"E25.left"),sQuery(id+"F8.wireOp",EDGE,"E25.right"),sQuery(id+"F8.wireOp",EDGE,"E27.top"),sQuery(id+"F8.wireOp",EDGE,"E27.left"),sQuery(id+"F8.wireOp",EDGE,"E27.right")])],"isStart":false})});
            var sketch = newSketch(context, id + "F26", { "sketchPlane" : qUnion([Q0])});
            skLineSegment(sketch, "E67.bottom", {"start": v(-48, 37.5) * mm, "end": v(-32, 37.5) * mm});
            skLineSegment(sketch, "E67.top", {"start": v(-48, 34.5) * mm, "end": v(-32, 34.5) * mm});
            skLineSegment(sketch, "E67.left", {"start": v(-48, 37.5) * mm, "end": v(-48, 34.5) * mm});
            skLineSegment(sketch, "E67.right", {"start": v(-32, 37.5) * mm, "end": v(-32, 34.5) * mm});
            skLineSegment(sketch, "E68.bottom", {"start": v(32, 37.5) * mm, "end": v(48, 37.5) * mm});
            skLineSegment(sketch, "E68.top", {"start": v(32, 34.5) * mm, "end": v(48, 34.5) * mm});
            skLineSegment(sketch, "E68.left", {"start": v(32, 37.5) * mm, "end": v(32, 34.5) * mm});
            skLineSegment(sketch, "E68.right", {"start": v(48, 37.5) * mm, "end": v(48, 34.5) * mm});
            skSolve(sketch);
        }
        {
            var Q0;
            Q0 = qSketchRegion(id + "F26", true);
            extrude(context, id + "F27", {"entities" : qUnion([Q0]), "operationType" : NewBodyOperationType.REMOVE, "oppositeDirection" : true, "depth" : 3 * mm});
        }
        {
            var Q0;
            Q0=makeQuery(id+"F11.opExtrude","CAP_EDGE",EDGE,{"disambiguationData":[OSD([sQuery(id+"F10.wireOp",EDGE,"E29.right")])],"isStart":false});
            var Q1;
            Q1=makeQuery(id+"F11.opExtrude","CAP_EDGE",EDGE,{"disambiguationData":[OSD([sQuery(id+"F10.wireOp",EDGE,"E29.top")])],"isStart":false});
            var Q2;
            Q2=makeQuery(id+"F11.opExtrude","CAP_EDGE",EDGE,{"disambiguationData":[OSD([sQuery(id+"F10.wireOp",EDGE,"E29.left")])],"isStart":false});
            var Q3;
            Q3=makeQuery(id+"F11.opExtrude","CAP_EDGE",EDGE,{"disambiguationData":[OSD([sQuery(id+"F10.wireOp",EDGE,"E29.bottom")])],"isStart":false});
            fillet(context, id + "F28", {"entities" : qUnion([Q0, Q1, Q2, Q3]), "radius" : 0.5 * mm, "tangentPropagation" : true, "allowEdgeOverflow" : false});
        }
        {
            var Q0;
            Q0=makeQuery(id+"F21.opExtrude","SWEPT_FACE",FACE,{"disambiguationData":[OSD([sQuery(id+"F20.wireOp",EDGE,"E58.left")])]});
            var sketch = newSketch(context, id + "F29", { "sketchPlane" : qUnion([Q0])});
            skLineSegment(sketch, "E69.bottom", {"start": v(34.5, -5) * mm, "end": v(14.5, -5) * mm});
            skLineSegment(sketch, "E69.top", {"start": v(34.5, -10) * mm, "end": v(14.5, -10) * mm});
            skLineSegment(sketch, "E69.left", {"start": v(34.5, -5) * mm, "end": v(34.5, -10) * mm});
            skLineSegment(sketch, "E69.right", {"start": v(14.5, -5) * mm, "end": v(14.5, -10) * mm});
            skSolve(sketch);
        }
        {
            var Q0;
            Q0=makeQuery(id+"F21.boolean.opBoolean","MERGE",FACE,{"derivedFrom":[makeQuery(id+"F5.boolean.opBoolean","COPY",FACE,{"derivedFrom":makeQuery(id+"F5.opExtrude","SWEPT_FACE",FACE,{"disambiguationData":[OSD([sQuery(id+"F4.wireOp",EDGE,"E19.right")])]})}),makeQuery(id+"F21.opExtrude","SWEPT_FACE",FACE,{"disambiguationData":[OSD([sQuery(id+"F20.wireOp",EDGE,"E59.left")])]})]});
            var sketch = newSketch(context, id + "F30", { "sketchPlane" : qUnion([Q0])});
            skLineSegment(sketch, "E70.bottom", {"start": v(34.5, -5) * mm, "end": v(14.5, -5) * mm});
            skLineSegment(sketch, "E70.top", {"start": v(34.5, -10) * mm, "end": v(14.5, -10) * mm});
            skLineSegment(sketch, "E70.left", {"start": v(34.5, -5) * mm, "end": v(34.5, -10) * mm});
            skLineSegment(sketch, "E70.right", {"start": v(14.5, -5) * mm, "end": v(14.5, -10) * mm});
            skSolve(sketch);
        }
        {
            var Q0;
            Q0=makeQuery(id+"F30.imprint","IMPRINT",FACE,{"disambiguationData":[TD([[makeQuery(id+"F30.imprint","IMPRINT",EDGE,{"derivedFrom":sQuery(id+"F30.wireOp",EDGE,"E70.bottom")}),1.0]])]});
            var Q1;
            Q1=makeQuery(id+"F29.imprint","IMPRINT",FACE,{"disambiguationData":[TD([[makeQuery(id+"F29.imprint","IMPRINT",EDGE,{"derivedFrom":sQuery(id+"F29.wireOp",EDGE,"E69.bottom")}),1.0]])]});
            extrude(context, id + "F31", {"entities" : qUnion([Q0, Q1]), "operationType" : NewBodyOperationType.REMOVE, "oppositeDirection" : true, "depth" : 4 * mm});
        }
        {
            var Q0;
            Q0=makeQuery(id+"F31.boolean.opBoolean","COPY",FACE,{"derivedFrom":makeQuery(id+"F31.opExtrude","SWEPT_FACE",FACE,{"disambiguationData":[OSD([sQuery(id+"F29.wireOp",EDGE,"E69.bottom")])]})});
            var sketch = newSketch(context, id + "F32", { "sketchPlane" : qUnion([Q0])});
            skLineSegment(sketch, "E71.bottom", {"start": v(-15, -34.5) * mm, "end": v(-13, -34.5) * mm});
            skLineSegment(sketch, "E71.top", {"start": v(-15, -14.5) * mm, "end": v(-13, -14.5) * mm});
            skLineSegment(sketch, "E71.left", {"start": v(-15, -34.5) * mm, "end": v(-15, -14.5) * mm});
            skLineSegment(sketch, "E71.right", {"start": v(-13, -34.5) * mm, "end": v(-13, -14.5) * mm});
            skSolve(sketch);
        }
        {
            var Q0;
            Q0 = qSketchRegion(id + "F32", true);
            extrude(context, id + "F33", {"entities" : qUnion([Q0]), "operationType" : NewBodyOperationType.REMOVE, "oppositeDirection" : true, "depth" : 0.5 * mm});
        }
    });
